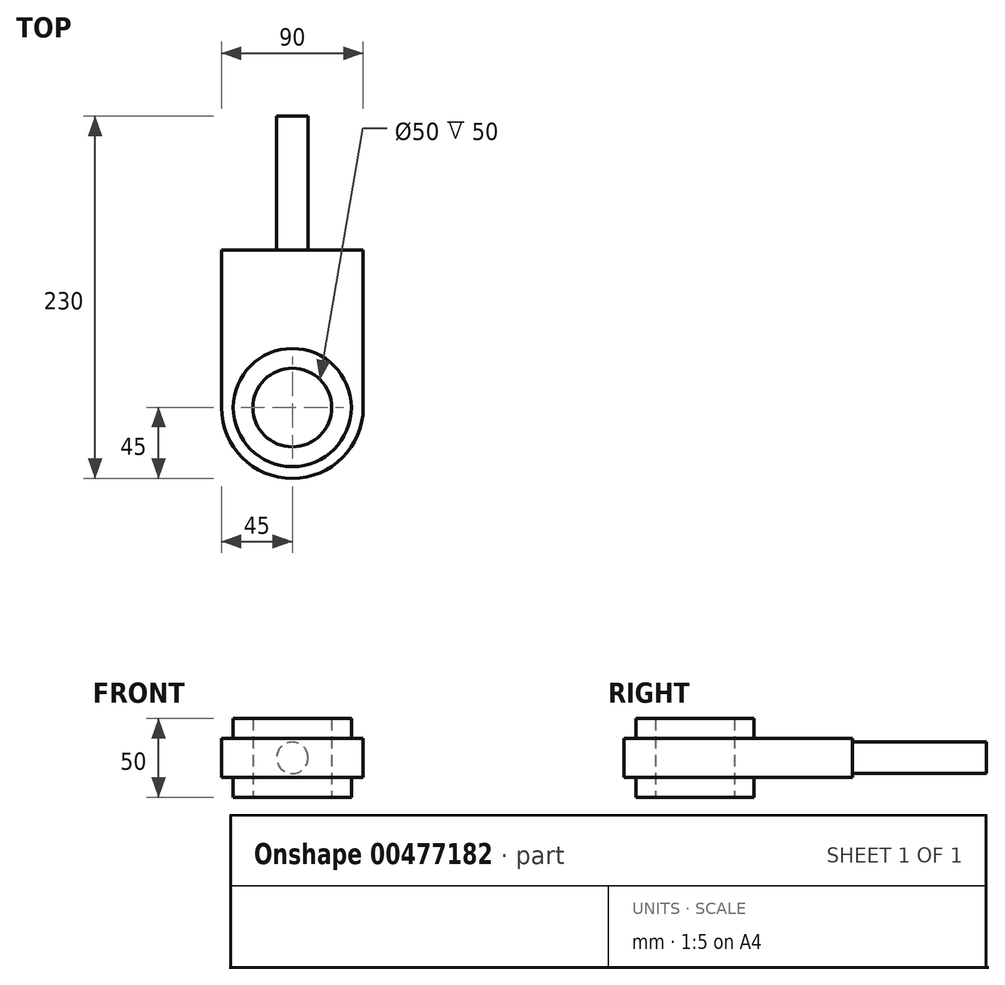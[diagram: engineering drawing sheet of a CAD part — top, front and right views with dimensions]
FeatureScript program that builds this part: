
annotation { "Feature Type Name" : "Feature", "Feature Type Description" : "" }
export const myFeature = defineFeature(function(context is Context, id is Id, definition is map)
    precondition{}
    {
        {
            var Q0;
            Q0=qCreatedBy(makeId("Top.planeOp"),FACE);
            var sketch = newSketch(context, id + "F0", { "sketchPlane" : qUnion([Q0])});
            skCircle(sketch, "E0", {"center": v(0, 0) * mm, "radius": 25 * mm});
            skCircle(sketch, "E1", {"center": v(0, 0) * mm, "radius": 37.5 * mm});
            skArc(sketch, "E2", {"start": v(-45, 0) * mm, "mid": v(0, -45) * mm, "end": v(45, 0) * mm});
            skLineSegment(sketch, "E3", {"start": v(-45, 0) * mm, "end": v(-45, 100) * mm});
            skLineSegment(sketch, "E4", {"start": v(-45, 100) * mm, "end": v(45, 100) * mm});
            skLineSegment(sketch, "E5", {"start": v(45, 0) * mm, "end": v(45, 100) * mm});
            skSolve(sketch);
        }
        {
            var Q0;
            Q0=makeQuery(id+"F0.imprint","IMPRINT",FACE,{"disambiguationData":[TD([[makeQuery(id+"F0.imprint","IMPRINT",EDGE,{"derivedFrom":sQuery(id+"F0.wireOp",EDGE,"E0")}),-1.0]])]});
            extrude(context, id + "F1", {"entities" : qUnion([Q0]), "endBound" : BoundingType.SYMMETRIC, "depth" : 50 * mm});
        }
        {
            var Q0;
            Q0 = qSketchRegion(id + "F0", true);
            extrude(context, id + "F2", {"entities" : qUnion([Q0]), "operationType" : NewBodyOperationType.ADD, "endBound" : BoundingType.SYMMETRIC, "depth" : 25 * mm});
        }
        {
            var Q0;
            Q0=makeQuery(id+"F2.opExtrude","SWEPT_FACE",FACE,{"disambiguationData":[OSD([sQuery(id+"F0.wireOp",EDGE,"E4")])]});
            var sketch = newSketch(context, id + "F3", { "sketchPlane" : qUnion([Q0])});
            skCircle(sketch, "E6", {"center": v(0, 0) * mm, "radius": 10 * mm});
            skSolve(sketch);
        }
        {
            var Q0;
            Q0 = qSketchRegion(id + "F3", true);
            extrude(context, id + "F4", {"entities" : qUnion([Q0]), "operationType" : NewBodyOperationType.ADD, "depth" : (230 - 145) * mm});
        }
    });
